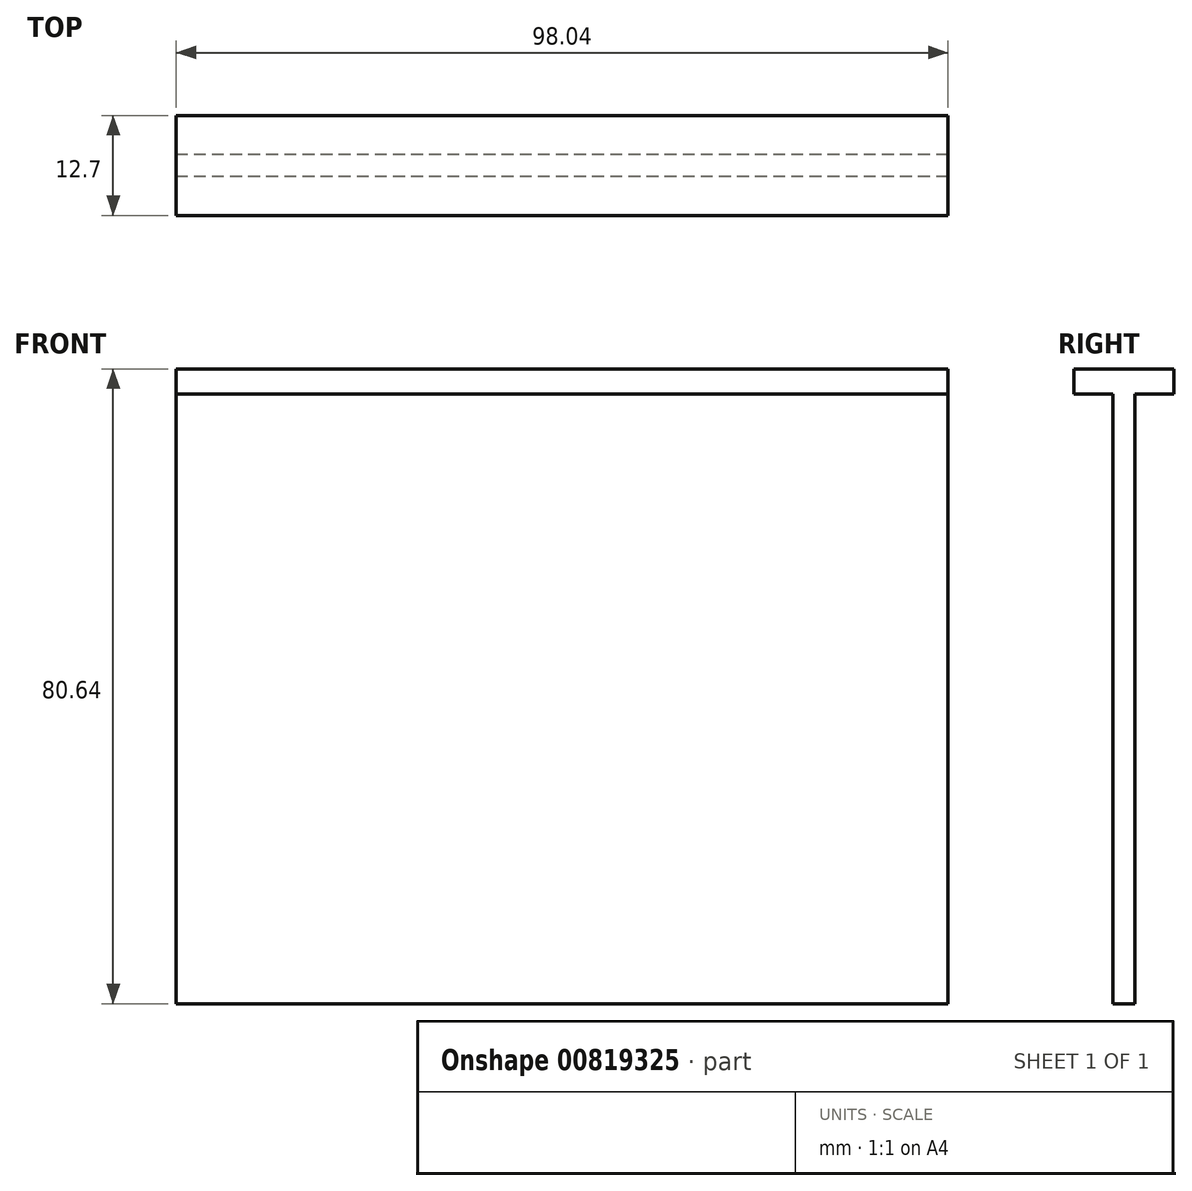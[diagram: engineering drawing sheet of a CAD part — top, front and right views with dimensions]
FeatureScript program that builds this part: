
annotation { "Feature Type Name" : "Feature", "Feature Type Description" : "" }
export const myFeature = defineFeature(function(context is Context, id is Id, definition is map)
    precondition{}
    {
        {
            var Q0;
            Q0=qCreatedBy(makeId("Right.planeOp"),FACE);
            var sketch = newSketch(context, id + "F0", { "sketchPlane" : qUnion([Q0])});
            skLineSegment(sketch, "E0", {"start": v(0, 0) * mm, "end": v(0, 3.17) * mm});
            skLineSegment(sketch, "E1", {"start": v(0, 3.17) * mm, "end": v(12.7, 3.17) * mm});
            skLineSegment(sketch, "E2", {"start": v(12.7, 3.17) * mm, "end": v(12.7, 0) * mm});
            skLineSegment(sketch, "E3", {"start": v(12.7, 0) * mm, "end": v(7.75, 0) * mm});
            skLineSegment(sketch, "E4", {"start": v(7.75, 0) * mm, "end": v(7.75, -77.47) * mm});
            skLineSegment(sketch, "E5", {"start": v(7.75, -77.47) * mm, "end": v(4.95, -77.47) * mm});
            skLineSegment(sketch, "E6", {"start": v(4.95, -77.47) * mm, "end": v(4.95, 0) * mm});
            skLineSegment(sketch, "E7", {"start": v(4.95, 0) * mm, "end": v(0, 0) * mm});
            skSolve(sketch);
        }
        {
            var Q0;
            Q0=qSketchRegion(id+"F0",true);
            extrude(context, id + "F1", {"entities" : qUnion([Q0]), "depth" : 98.04 * mm, "offsetDistance" : 25.4 * mm});
        }
    });
